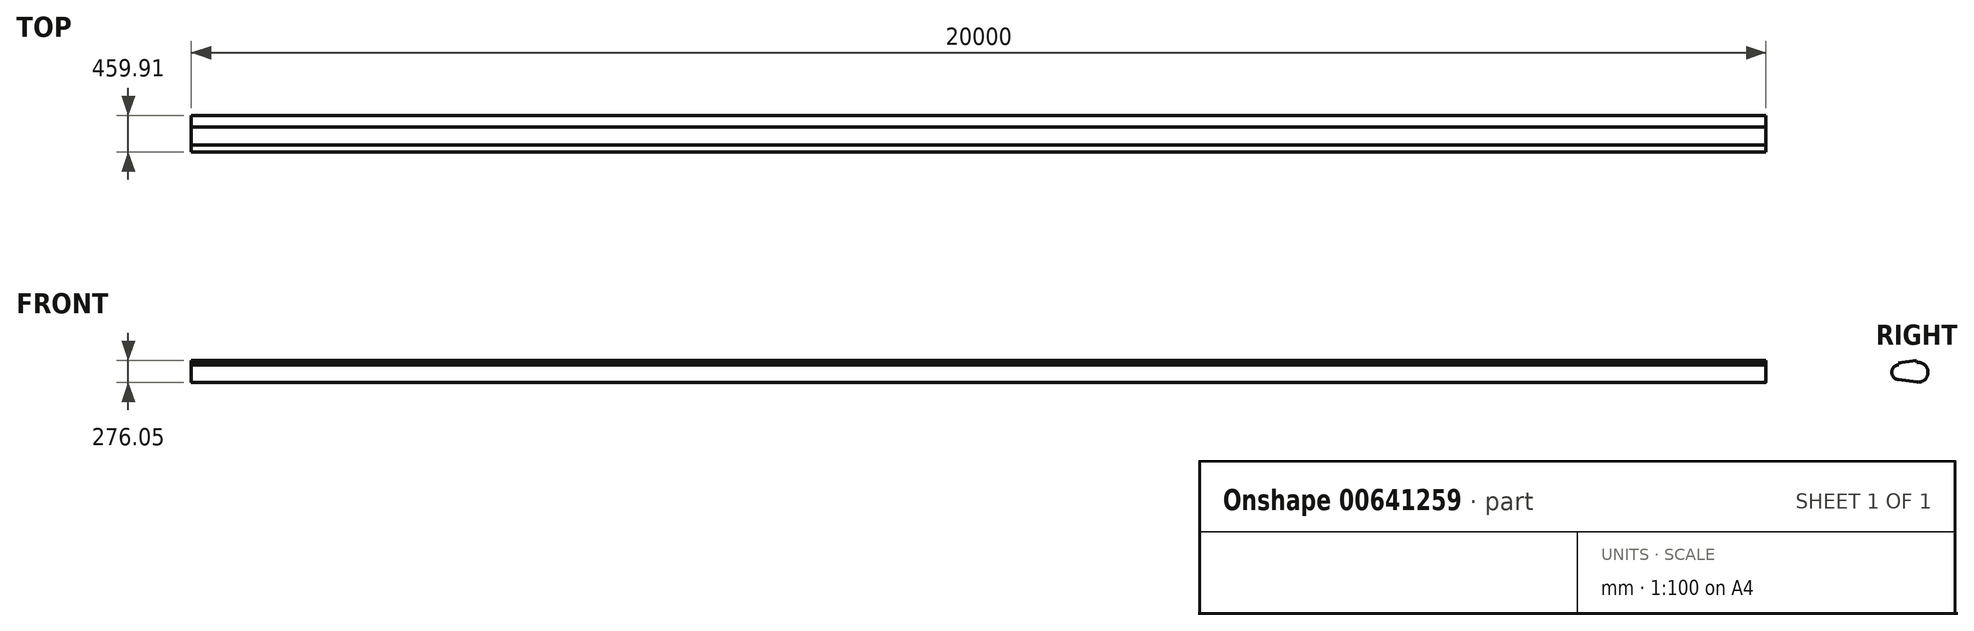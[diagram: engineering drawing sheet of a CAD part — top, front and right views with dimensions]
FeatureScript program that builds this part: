
annotation { "Feature Type Name" : "Feature", "Feature Type Description" : "" }
export const myFeature = defineFeature(function(context is Context, id is Id, definition is map)
    precondition{}
    {
        {
            var Q0;
            Q0=qCreatedBy(makeId("Right.planeOp"),FACE);
            var sketch = newSketch(context, id + "F0", { "sketchPlane" : qUnion([Q0])});
            skCircle(sketch, "E0", {"center": v(-98.4, 0) * mm, "radius": 93.7 * mm});
            skCircle(sketch, "E1", {"center": v(141.78, 0) * mm, "radius": 126.03 * mm});
            skLineSegment(sketch, "E2", {"start": v(124.82, -124.88) * mm, "end": v(-111, -92.85) * mm});
            skLineSegment(sketch, "E3", {"start": v(-111, -92.85) * mm, "end": v(-111, -92.85) * mm});
            skLineSegment(sketch, "E4", {"start": v(-118.74, 91.47) * mm, "end": v(124.65, 124.86) * mm});
            skSolve(sketch);
        }
        {
            var Q0;
            Q0 = qSketchRegion(id + "F0", true);
            extrude(context, id + "F1", {"entities" : qUnion([Q0]), "depth" : 20000 * mm, "offsetDistance" : 25.4 * mm});
        }
        {
            var Q0;
            Q0=makeQuery(id+"F1.opExtrude","SWEPT_FACE",FACE,{"disambiguationData":[OSD([sQuery(id+"F0.wireOp",EDGE,"E4")])]});
            extrude(context, id + "F2", {"entities" : qUnion([Q0]), "operationType" : NewBodyOperationType.ADD, "depth" : 25.4 * mm, "offsetDistance" : 25.4 * mm});
        }
    });
